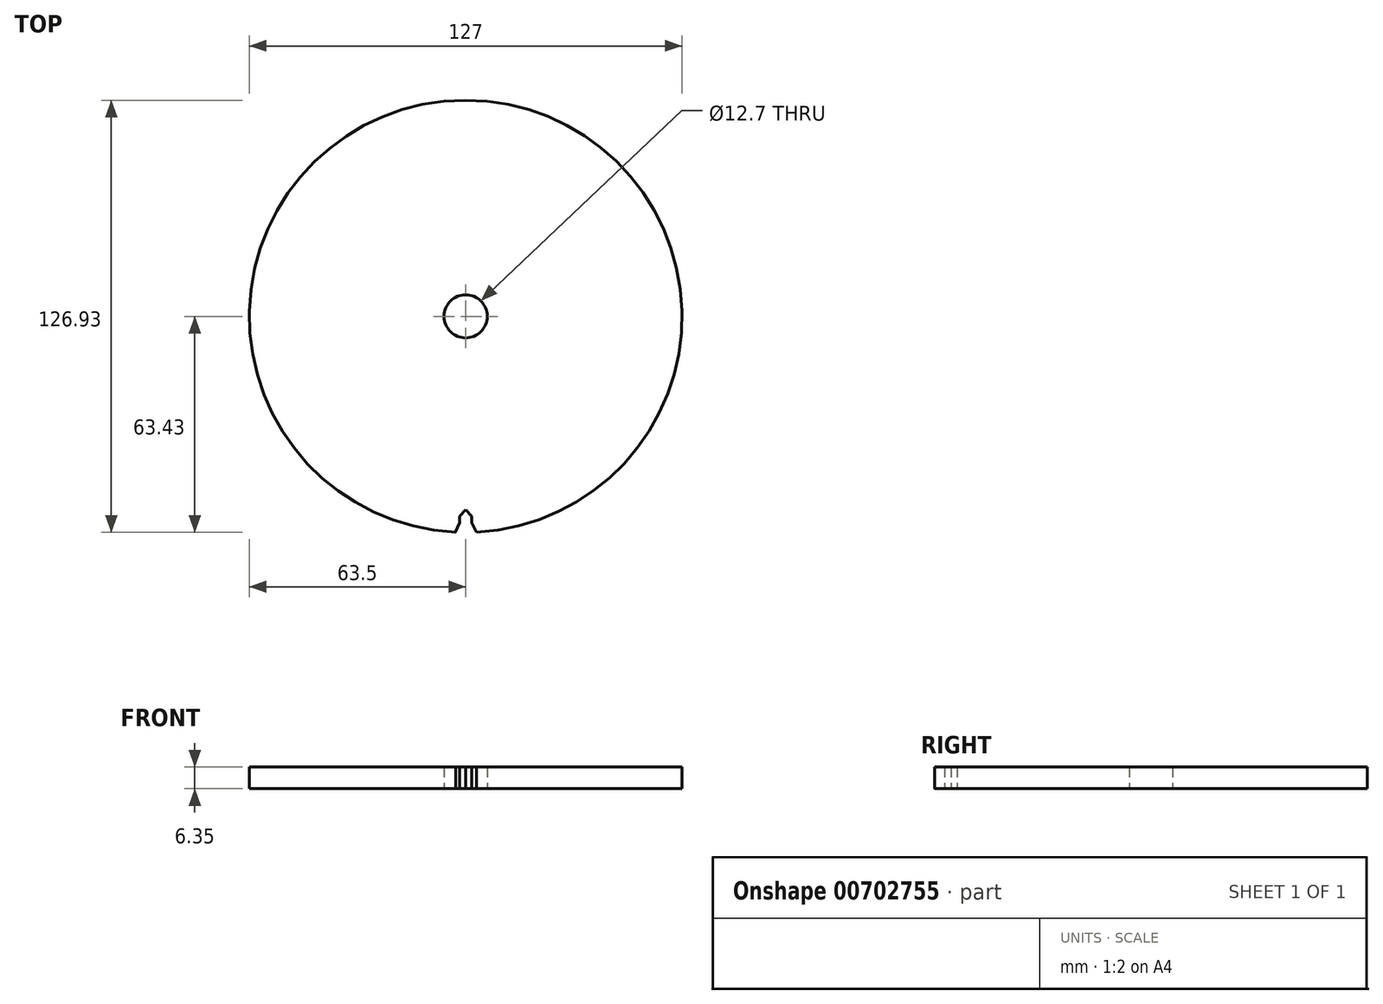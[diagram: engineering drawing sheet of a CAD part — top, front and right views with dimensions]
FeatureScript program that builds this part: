
annotation { "Feature Type Name" : "Feature", "Feature Type Description" : "" }
export const myFeature = defineFeature(function(context is Context, id is Id, definition is map)
    precondition{}
    {
        {
            var Q0;
            Q0=qCreatedBy(makeId("Top.planeOp"),FACE);
            var sketch = newSketch(context, id + "F0", { "sketchPlane" : qUnion([Q0])});
            skCircle(sketch, "E0", {"center": v(0, 0) * mm, "radius": 63.5 * mm});
            skSolve(sketch);
        }
        {
            var Q0;
            Q0 = qSketchRegion(id + "F0", true);
            extrude(context, id + "F1", {"entities" : qUnion([Q0]), "depth" : 6.35 * mm, "offsetDistance" : 25.4 * mm});
        }
        {
            var Q0;
            Q0=qCreatedBy(makeId("Top.planeOp"),FACE);
            var sketch = newSketch(context, id + "F2", { "sketchPlane" : qUnion([Q0])});
            skCircle(sketch, "E1", {"center": v(0, 0) * mm, "radius": 6.35 * mm});
            skSolve(sketch);
        }
        {
            var Q0;
            Q0 = qSketchRegion(id + "F2", true);
            extrude(context, id + "F3", {"entities" : qUnion([Q0]), "operationType" : NewBodyOperationType.REMOVE, "depth" : 25.4 * mm, "offsetDistance" : 25.4 * mm});
        }
        {
            var Q0;
            Q0=qCreatedBy(makeId("Top.planeOp"),FACE);
            var sketch = newSketch(context, id + "F4", { "sketchPlane" : qUnion([Q0])});
            skLineSegment(sketch, "E2", {"start": v(1.72, -58.68) * mm, "end": v(1.72, -60.58) * mm});
            skLineSegment(sketch, "E3", {"start": v(1.72, -60.58) * mm, "end": v(3.15, -63.42) * mm});
            skLineSegment(sketch, "E4", {"start": v(-1.72, -58.68) * mm, "end": v(-1.72, -60.58) * mm});
            skLineSegment(sketch, "E5", {"start": v(-1.72, -60.58) * mm, "end": v(-3, -63.42) * mm});
            skLineSegment(sketch, "E6", {"start": v(0, -56.8) * mm, "end": v(-1.72, -58.68) * mm});
            skLineSegment(sketch, "E7", {"start": v(0, -56.8) * mm, "end": v(1.72, -58.68) * mm});
            skFitSpline(sketch, "E8", {"points": [v(-3, -63.42) * mm, v(0, -64.42) * mm, v(3.15, -63.42) * mm], "startDerivative": vector(6.02, -3) * mm, "endDerivative": vector(6.27, 2.99) * mm});
            skSolve(sketch);
        }
        {
            var Q0;
            Q0 = qSketchRegion(id + "F4", true);
            extrude(context, id + "F5", {"entities" : qUnion([Q0]), "operationType" : NewBodyOperationType.REMOVE, "depth" : 25.4 * mm, "offsetDistance" : 25.4 * mm});
        }
    });
